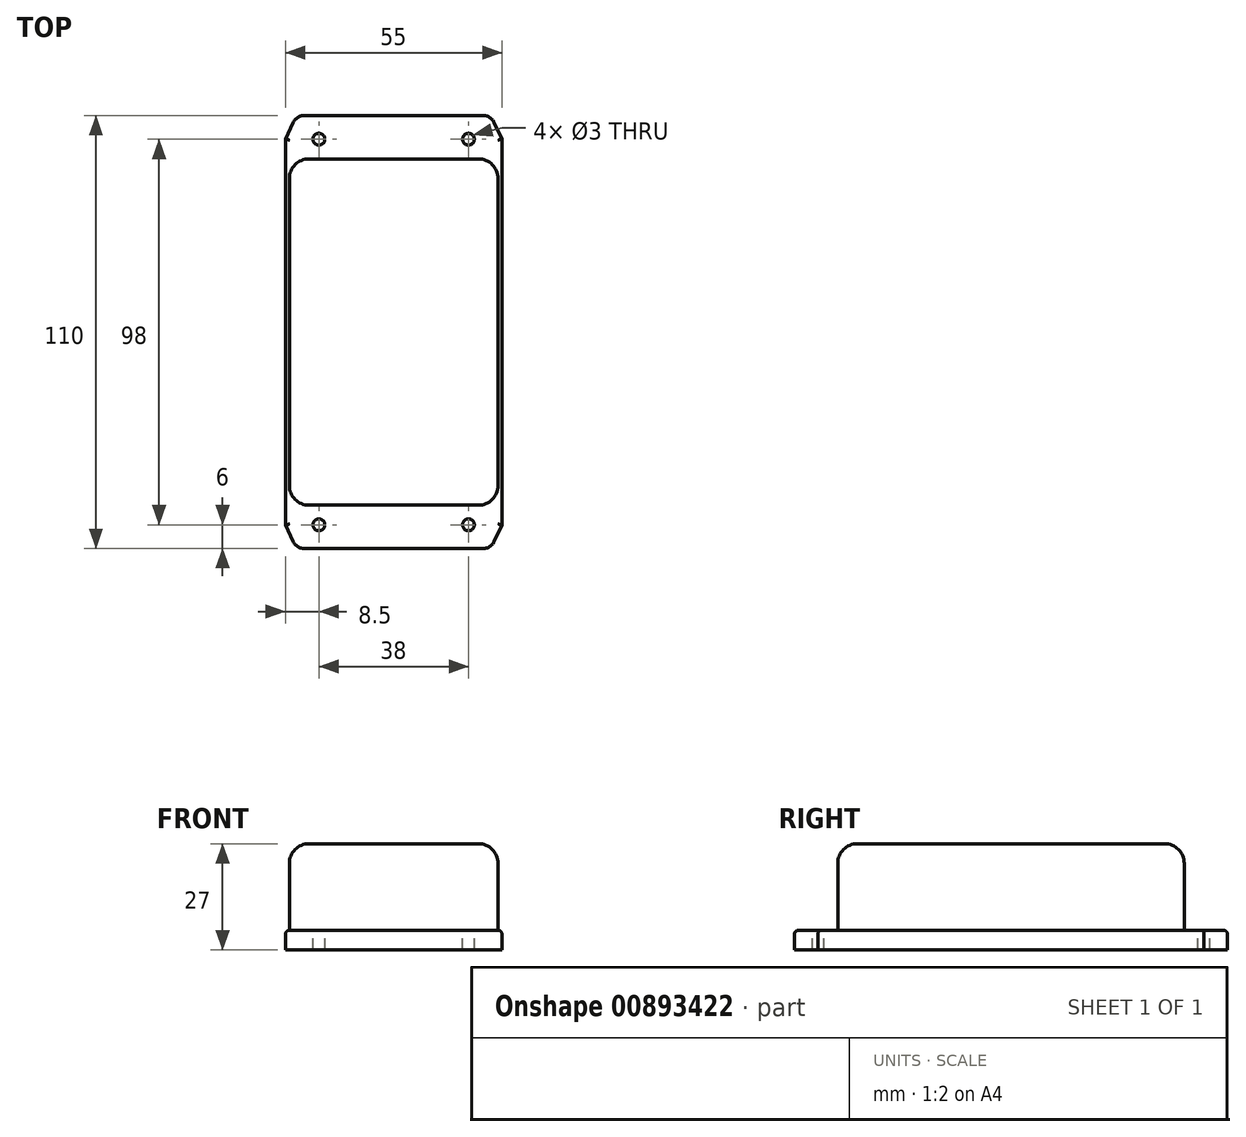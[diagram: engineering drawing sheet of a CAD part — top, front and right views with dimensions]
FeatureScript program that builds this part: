
annotation { "Feature Type Name" : "Feature", "Feature Type Description" : "" }
export const myFeature = defineFeature(function(context is Context, id is Id, definition is map)
    precondition{}
    {
        {
            var Q0;
            Q0=qCreatedBy(makeId("Top.planeOp"),FACE);
            var sketch = newSketch(context, id + "F0", { "sketchPlane" : qUnion([Q0])});
            skLineSegment(sketch, "E0.bottom", {"start": v(-22.8, 55) * mm, "end": v(22.8, 55) * mm});
            skLineSegment(sketch, "E0.top", {"start": v(-22.8, -55) * mm, "end": v(22.8, -55) * mm});
            skLineSegment(sketch, "E0.left", {"start": v(-27.5, 49) * mm, "end": v(-27.5, -49) * mm});
            skLineSegment(sketch, "E0.right", {"start": v(27.5, 49) * mm, "end": v(27.5, -49) * mm});
            skLineSegment(sketch, "E1", {"start": v(-27.5, -49) * mm, "end": v(-25.5, -53.27) * mm});
            skLineSegment(sketch, "E2", {"start": v(27.5, -49) * mm, "end": v(25.5, -53.27) * mm});
            skLineSegment(sketch, "E3", {"start": v(-27.5, 49) * mm, "end": v(-25.5, 53.27) * mm});
            skLineSegment(sketch, "E4", {"start": v(27.5, 49) * mm, "end": v(25.5, 53.27) * mm});
            skPoint(sketch, "E5.visualSharp", {"position": v(-24.7, 55) * mm});
            skArc(sketch, "E5.filletArc", {"start": v(-22.8, 55) * mm, "mid": v(-24.4, 54.53) * mm, "end": v(-25.5, 53.27) * mm});
            skPoint(sketch, "E6.visualSharp", {"position": v(24.7, 55) * mm});
            skArc(sketch, "E6.filletArc", {"start": v(25.5, 53.27) * mm, "mid": v(24.4, 54.53) * mm, "end": v(22.8, 55) * mm});
            skPoint(sketch, "E7.visualSharp", {"position": v(-24.7, -55) * mm});
            skArc(sketch, "E7.filletArc", {"start": v(-25.5, -53.27) * mm, "mid": v(-24.4, -54.53) * mm, "end": v(-22.8, -55) * mm});
            skPoint(sketch, "E8.visualSharp", {"position": v(24.7, -55) * mm});
            skArc(sketch, "E8.filletArc", {"start": v(22.8, -55) * mm, "mid": v(24.4, -54.53) * mm, "end": v(25.5, -53.27) * mm});
            skSolve(sketch);
        }
        {
            var Q0;
            Q0=makeQuery(id+"F0.imprint","IMPRINT",FACE,{"disambiguationData":[TD([[makeQuery(id+"F0.imprint","IMPRINT",EDGE,{"derivedFrom":sQuery(id+"F0.wireOp",EDGE,"E0.bottom")}),-1.0]])]});
            extrude(context, id + "F1", {"entities" : qUnion([Q0]), "depth" : 5 * mm, "offsetDistance" : 25 * mm});
        }
        {
            var Q0;
            Q0=makeQuery(id+"F1.opExtrude","CAP_FACE",FACE,{"disambiguationData":[OSD([sQuery(id+"F0.wireOp",EDGE,"E0.bottom"),sQuery(id+"F0.wireOp",EDGE,"E0.top"),sQuery(id+"F0.wireOp",EDGE,"E0.left"),sQuery(id+"F0.wireOp",EDGE,"E0.right"),sQuery(id+"F0.wireOp",EDGE,"E1"),sQuery(id+"F0.wireOp",EDGE,"E2"),sQuery(id+"F0.wireOp",EDGE,"E3"),sQuery(id+"F0.wireOp",EDGE,"E4"),sQuery(id+"F0.wireOp",EDGE,"E5.filletArc"),sQuery(id+"F0.wireOp",EDGE,"E6.filletArc"),sQuery(id+"F0.wireOp",EDGE,"E7.filletArc"),sQuery(id+"F0.wireOp",EDGE,"E8.filletArc")])],"isStart":false});
            var sketch = newSketch(context, id + "F2", { "sketchPlane" : qUnion([Q0])});
            skLineSegment(sketch, "E9.bottom", {"start": v(-26.5, 44) * mm, "end": v(26.5, 44) * mm});
            skLineSegment(sketch, "E9.top", {"start": v(-26.5, -44) * mm, "end": v(26.5, -44) * mm});
            skLineSegment(sketch, "E9.left", {"start": v(-26.5, 44) * mm, "end": v(-26.5, -44) * mm});
            skLineSegment(sketch, "E9.right", {"start": v(26.5, 44) * mm, "end": v(26.5, -44) * mm});
            skSolve(sketch);
        }
        {
            var Q0;
            Q0=makeQuery(id+"F2.imprint","IMPRINT",FACE,{"disambiguationData":[TD([[makeQuery(id+"F2.imprint","IMPRINT",EDGE,{"derivedFrom":sQuery(id+"F2.wireOp",EDGE,"E9.bottom")}),-1.0]])]});
            extrude(context, id + "F3", {"entities" : qUnion([Q0]), "operationType" : NewBodyOperationType.ADD, "depth" : 22 * mm, "offsetDistance" : 25 * mm});
        }
        {
            var Q0;
            Q0=makeQuery(id+"F1.opExtrude","CAP_FACE",FACE,{"disambiguationData":[OSD([sQuery(id+"F0.wireOp",EDGE,"E0.bottom"),sQuery(id+"F0.wireOp",EDGE,"E0.top"),sQuery(id+"F0.wireOp",EDGE,"E0.left"),sQuery(id+"F0.wireOp",EDGE,"E0.right"),sQuery(id+"F0.wireOp",EDGE,"E1"),sQuery(id+"F0.wireOp",EDGE,"E2"),sQuery(id+"F0.wireOp",EDGE,"E3"),sQuery(id+"F0.wireOp",EDGE,"E4"),sQuery(id+"F0.wireOp",EDGE,"E5.filletArc"),sQuery(id+"F0.wireOp",EDGE,"E6.filletArc"),sQuery(id+"F0.wireOp",EDGE,"E7.filletArc"),sQuery(id+"F0.wireOp",EDGE,"E8.filletArc")])],"isStart":false});
            var sketch = newSketch(context, id + "F4", { "sketchPlane" : qUnion([Q0])});
            skCircle(sketch, "E10", {"center": v(-19, 49) * mm, "radius": 1.5 * mm});
            skCircle(sketch, "E11", {"center": v(19, 49) * mm, "radius": 1.5 * mm});
            skCircle(sketch, "E12", {"center": v(-19, -49) * mm, "radius": 1.5 * mm});
            skCircle(sketch, "E13", {"center": v(19, -49) * mm, "radius": 1.5 * mm});
            skSolve(sketch);
        }
        {
            var Q0;
            Q0=makeQuery(id+"F4.imprint","IMPRINT",FACE,{"disambiguationData":[TD([[makeQuery(id+"F4.imprint","IMPRINT",EDGE,{"derivedFrom":sQuery(id+"F4.wireOp",EDGE,"E10")}),1.0]])]});
            var Q1;
            Q1=makeQuery(id+"F4.imprint","IMPRINT",FACE,{"disambiguationData":[TD([[makeQuery(id+"F4.imprint","IMPRINT",EDGE,{"derivedFrom":sQuery(id+"F4.wireOp",EDGE,"E11")}),1.0]])]});
            var Q2;
            Q2=makeQuery(id+"F4.imprint","IMPRINT",FACE,{"disambiguationData":[TD([[makeQuery(id+"F4.imprint","IMPRINT",EDGE,{"derivedFrom":sQuery(id+"F4.wireOp",EDGE,"E12")}),1.0]])]});
            var Q3;
            Q3=makeQuery(id+"F4.imprint","IMPRINT",FACE,{"disambiguationData":[TD([[makeQuery(id+"F4.imprint","IMPRINT",EDGE,{"derivedFrom":sQuery(id+"F4.wireOp",EDGE,"E13")}),1.0]])]});
            extrude(context, id + "F5", {"entities" : qUnion([Q0, Q1, Q2, Q3]), "operationType" : NewBodyOperationType.REMOVE, "oppositeDirection" : true, "depth" : 25 * mm, "offsetDistance" : 25 * mm});
        }
        {
            var Q0;
            Q0=makeQuery(id+"F3.opExtrude","CAP_EDGE",EDGE,{"disambiguationData":[OSD([sQuery(id+"F2.wireOp",EDGE,"E9.left")])],"isStart":false});
            var Q1;
            Q1=makeQuery(id+"F3.opExtrude","CAP_EDGE",EDGE,{"disambiguationData":[OSD([sQuery(id+"F2.wireOp",EDGE,"E9.bottom")])],"isStart":false});
            var Q2;
            Q2=makeQuery(id+"F3.opExtrude","CAP_EDGE",EDGE,{"disambiguationData":[OSD([sQuery(id+"F2.wireOp",EDGE,"E9.right")])],"isStart":false});
            var Q3;
            Q3=makeQuery(id+"F3.opExtrude","CAP_EDGE",EDGE,{"disambiguationData":[OSD([sQuery(id+"F2.wireOp",EDGE,"E9.top")])],"isStart":false});
            var Q4;
            Q4=makeQuery(id+"F3.opExtrude","SWEPT_EDGE",EDGE,{"disambiguationData":[OSD([sQuery(id+"F2.wireOp",EDGE,"E9.top"),sQuery(id+"F2.wireOp",EDGE,"E9.right")])]});
            var Q5;
            Q5=makeQuery(id+"F3.opExtrude","SWEPT_EDGE",EDGE,{"disambiguationData":[OSD([sQuery(id+"F2.wireOp",EDGE,"E9.bottom"),sQuery(id+"F2.wireOp",EDGE,"E9.right")])]});
            var Q6;
            Q6=makeQuery(id+"F3.opExtrude","SWEPT_EDGE",EDGE,{"disambiguationData":[OSD([sQuery(id+"F2.wireOp",EDGE,"E9.bottom"),sQuery(id+"F2.wireOp",EDGE,"E9.left")])]});
            var Q7;
            Q7=makeQuery(id+"F3.opExtrude","SWEPT_EDGE",EDGE,{"disambiguationData":[OSD([sQuery(id+"F2.wireOp",EDGE,"E9.top"),sQuery(id+"F2.wireOp",EDGE,"E9.left")])]});
            fillet(context, id + "F6", {"entities" : qUnion([Q0, Q1, Q2, Q3, Q4, Q5, Q6, Q7]), "tangentPropagation" : true, "radius" : 5 * mm, "defaultsChanged" : false, "vertexSettings" : [], "allowEdgeOverflow" : false});
        }
        {
            var Q0;
            Q0=makeQuery(id+"F1.opExtrude","CAP_EDGE",EDGE,{"disambiguationData":[OSD([sQuery(id+"F0.wireOp",EDGE,"E0.right")])],"isStart":false});
            var Q1;
            Q1=makeQuery(id+"F1.opExtrude","CAP_EDGE",EDGE,{"disambiguationData":[OSD([sQuery(id+"F0.wireOp",EDGE,"E2")])],"isStart":false});
            var Q2;
            Q2=makeQuery(id+"F1.opExtrude","CAP_EDGE",EDGE,{"disambiguationData":[OSD([sQuery(id+"F0.wireOp",EDGE,"E4")])],"isStart":false});
            var Q3;
            Q3=makeQuery(id+"F1.opExtrude","CAP_EDGE",EDGE,{"disambiguationData":[OSD([sQuery(id+"F0.wireOp",EDGE,"E0.left")])],"isStart":false});
            fillet(context, id + "F7", {"entities" : qUnion([Q0, Q1, Q2, Q3]), "tangentPropagation" : true, "radius" : 1 * mm, "defaultsChanged" : false, "vertexSettings" : [], "allowEdgeOverflow" : false});
        }
    });
